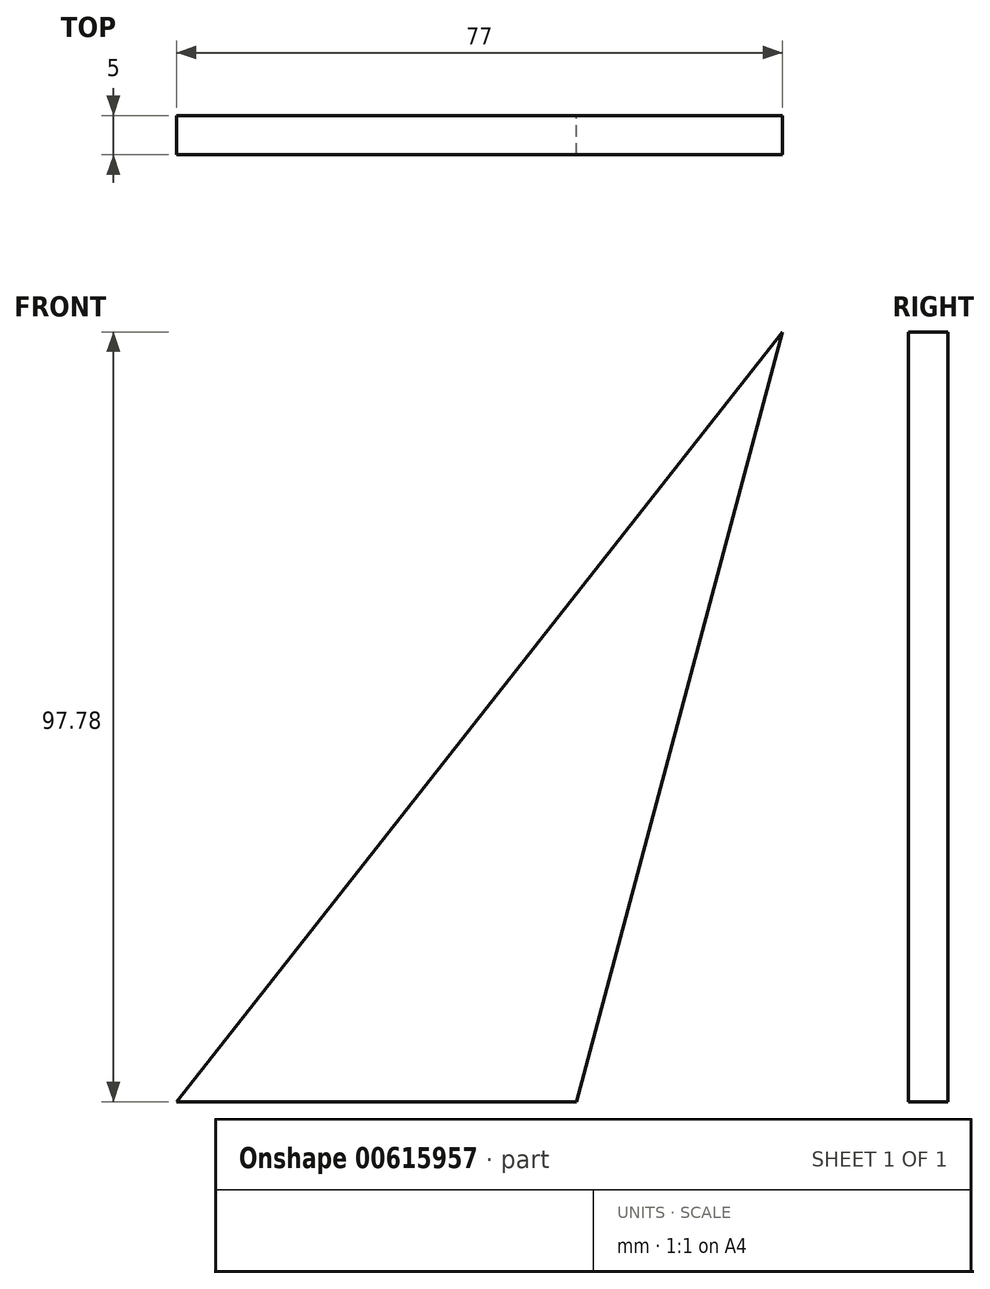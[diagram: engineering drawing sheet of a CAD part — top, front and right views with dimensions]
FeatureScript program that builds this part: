
annotation { "Feature Type Name" : "Feature", "Feature Type Description" : "" }
export const myFeature = defineFeature(function(context is Context, id is Id, definition is map)
    precondition{}
    {
        {
            var Q0;
            Q0=qCreatedBy(makeId("Front.planeOp"),FACE);
            var sketch = newSketch(context, id + "F0", { "sketchPlane" : qUnion([Q0])});
            skLineSegment(sketch, "E0", {"start": v(0, 0) * mm, "end": v(50.8, 0) * mm});
            skLineSegment(sketch, "E1", {"start": v(50.8, 0) * mm, "end": v(77, 97.78) * mm});
            skLineSegment(sketch, "E2", {"start": v(77, 97.78) * mm, "end": v(0, 0) * mm});
            skSolve(sketch);
        }
        {
            var Q0;
            Q0=makeQuery(id+"F0.imprint","IMPRINT",FACE,{"disambiguationData":[TD([[makeQuery(id+"F0.imprint","IMPRINT",EDGE,{"derivedFrom":sQuery(id+"F0.wireOp",EDGE,"E0")}),1.0]])]});
            extrude(context, id + "F1", {"entities" : qUnion([Q0]), "depth" : 5 * mm, "offsetDistance" : 25.4 * mm});
        }
    });
